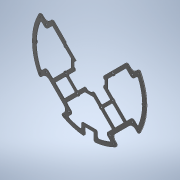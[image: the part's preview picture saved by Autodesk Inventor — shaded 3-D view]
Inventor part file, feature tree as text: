
AUTODESK INVENTOR PART (.ipt)
format: ipt  version: 2020 (Build 240168000, 168)  size: 1,571,328 bytes
history: native  units: mm
features: sketch x4, other x3, extrude x3, projected_geometry x3, fillet x2, chamfer x1
ambient origin geometry x8: Origin, YZ Plane, XZ Plane, XY Plane, X Axis, Y Axis, Z Axis, Center Point
bodies: Body1 (feature_tree)
feature tree (16):
  other  "Твердое тело1"
  other  "РабПлоскость2"
  sketch  "Эскиз1"
  other  "РабПлоскость1"
  sketch  "Эскиз3"
  extrude  "Выдавливание2"  Depth=0.5mm
  extrude  "Выдавливание3"  Depth=2.0mm TaperAngle=0.0deg
  fillet  "Сопряжение3"  Radius=0.9mm
  fillet  "Сопряжение4"  Radius=3.0mm
  extrude  "Выдавливание4"  Depth=3.0mm
  chamfer  "Фаска2"  Distance=2.0mm
  projected_geometry  "Спроецированная петля1"
  projected_geometry  "Спроецированная петля2"
  sketch  "Эскиз4"
  projected_geometry  "Спроецированная петля3"
  sketch  "Эскиз5"
